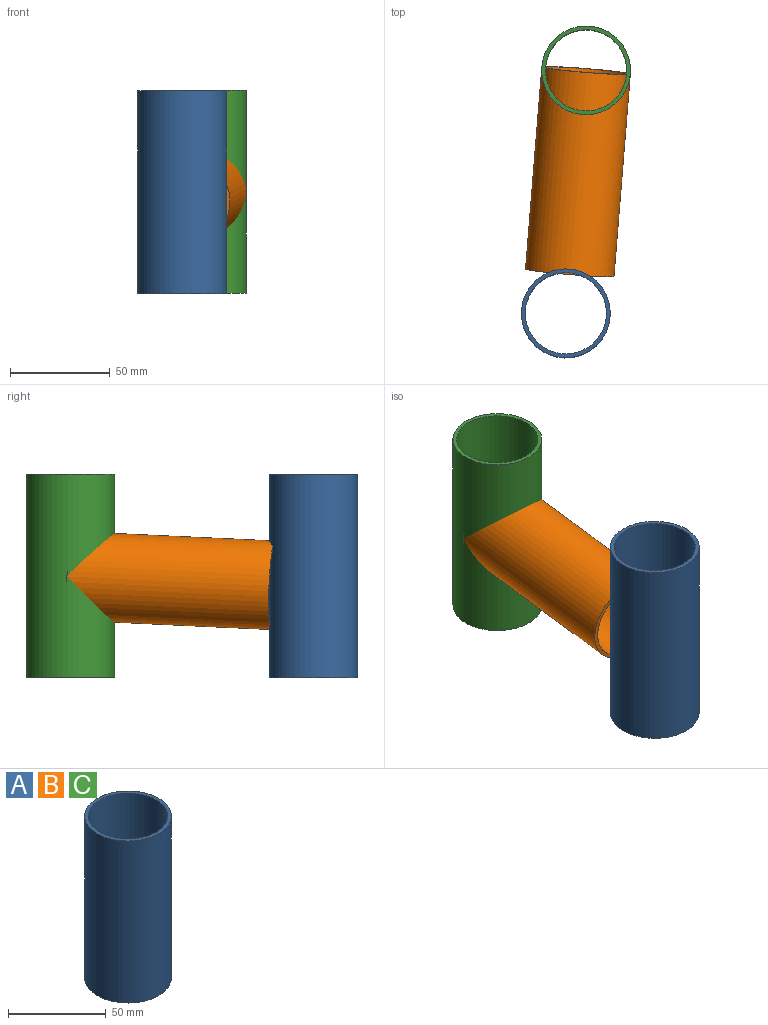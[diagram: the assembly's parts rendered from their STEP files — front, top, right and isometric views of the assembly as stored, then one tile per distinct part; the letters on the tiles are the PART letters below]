
ASSEMBLY  parts=3 mates=1
PART A: 4 faces, bbox 44.5x44.5x101.6 mm
  f0: cylinder r=20.32mm len=101.6mm, axis (0,0,-1), area 12971.7mm2, adj f2,f3
  f1: cylinder r=22.23mm len=101.6mm, axis (0,0,-1), area 14187.8mm2, adj f2,f3
  f2: plane 44.45x44.45mm, normal (0,0,1), area 254.6mm2, adj f0,f1
  f3: plane 44.45x44.45mm, normal (0,0,-1), area 254.6mm2, adj f0,f1
PART B: same geometry as A
PART C: same geometry as A
PLACE A t=(-10.15,-121.63,-50.99)mm
PLACE B rot(axis=(0.66,0.52,-0.54),118.8deg) t=(0,0,0)mm
PLACE C t=(0,0,-50.8)mm
MATE ball B.f1 <-> C.f1  axis (0.08,1,0.05) through (0,0,0)mm
